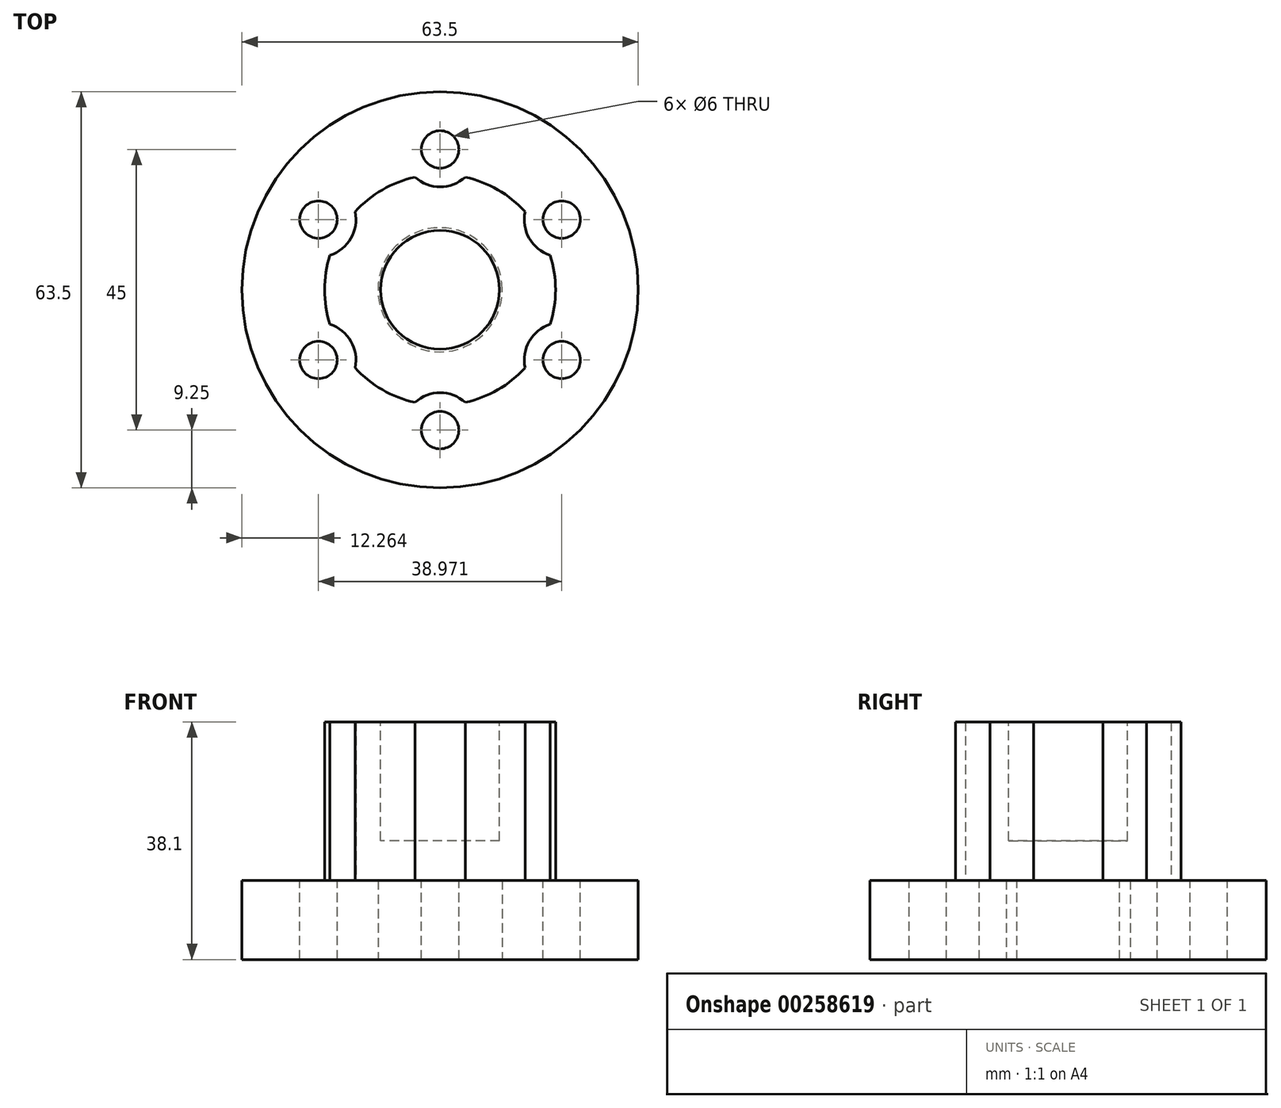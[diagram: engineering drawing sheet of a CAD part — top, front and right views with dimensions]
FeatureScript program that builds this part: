
annotation { "Feature Type Name" : "Feature", "Feature Type Description" : "" }
export const myFeature = defineFeature(function(context is Context, id is Id, definition is map)
    precondition{}
    {
        {
            var Q0;
            Q0=qCreatedBy(makeId("Top.planeOp"),FACE);
            var sketch = newSketch(context, id + "F0", { "sketchPlane" : qUnion([Q0])});
            skCircle(sketch, "E0", {"center": v(0, 0) * mm, "radius": 31.75 * mm});
            skSolve(sketch);
        }
        {
            var Q0;
            Q0=makeQuery(id+"F0.imprint","IMPRINT",FACE,{"disambiguationData":[TD([[makeQuery(id+"F0.imprint","IMPRINT",EDGE,{"derivedFrom":sQuery(id+"F0.wireOp",EDGE,"E0")}),1.0]])]});
            extrude(context, id + "F1", {"entities" : qUnion([Q0]), "depth" : 12.7 * mm});
        }
        {
            var Q0;
            Q0=makeQuery(id+"F1.opExtrude","CAP_FACE",FACE,{"disambiguationData":[OSD([sQuery(id+"F0.wireOp",EDGE,"E0")])],"isStart":false});
            var sketch = newSketch(context, id + "F2", { "sketchPlane" : qUnion([Q0])});
            skCircle(sketch, "E1", {"center": v(0, 0) * mm, "radius": 22.5 * mm, "construction": true});
            skCircle(sketch, "E2", {"center": v(0, 22.5) * mm, "radius": 3 * mm});
            skCircle(sketch, "E3.1.0", {"center": v(-19.49, 11.25) * mm, "radius": 3 * mm});
            skCircle(sketch, "E3.2.0", {"center": v(-19.49, -11.25) * mm, "radius": 3 * mm});
            skCircle(sketch, "E3.3.0", {"center": v(0, -22.5) * mm, "radius": 3 * mm});
            skCircle(sketch, "E3.4.0", {"center": v(19.49, -11.25) * mm, "radius": 3 * mm});
            skCircle(sketch, "E3.5.0", {"center": v(19.49, 11.25) * mm, "radius": 3 * mm});
            skSolve(sketch);
        }
        {
            var Q0;
            Q0 = qSketchRegion(id + "F2", true);
            extrude(context, id + "F3", {"entities" : qUnion([Q0]), "operationType" : NewBodyOperationType.REMOVE, "endBound" : BoundingType.THROUGH_ALL, "oppositeDirection" : true, "depth" : 25.4 * mm});
        }
        {
            var Q0;
            Q0=makeQuery(id+"F1.opExtrude","CAP_FACE",FACE,{"disambiguationData":[OSD([sQuery(id+"F0.wireOp",EDGE,"E0")])],"isStart":true});
            var sketch = newSketch(context, id + "F4", { "sketchPlane" : qUnion([Q0])});
            skCircle(sketch, "E4", {"center": v(0, 0) * mm, "radius": 9.95 * mm});
            skSolve(sketch);
        }
        {
            var Q0;
            Q0 = qSketchRegion(id + "F4", true);
            extrude(context, id + "F5", {"entities" : qUnion([Q0]), "operationType" : NewBodyOperationType.REMOVE, "oppositeDirection" : true, "depth" : 12.7 * mm});
        }
        {
            var Q0;
            Q0=makeQuery(id+"F1.opExtrude","CAP_FACE",FACE,{"disambiguationData":[OSD([sQuery(id+"F0.wireOp",EDGE,"E0")])],"isStart":false});
            var sketch = newSketch(context, id + "F6", { "sketchPlane" : qUnion([Q0])});
            skArc(sketch, "E5", {"start": v(4.03, -18.06) * mm, "mid": v(9.25, -16.02) * mm, "end": v(13.62, -12.52) * mm});
            skArc(sketch, "E6", {"start": v(4.03, -18.06) * mm, "mid": v(0, -16.5) * mm, "end": v(-4.03, -18.06) * mm});
            skArc(sketch, "E7.1.0", {"start": v(17.65, -5.54) * mm, "mid": v(14.29, -8.25) * mm, "end": v(13.62, -12.52) * mm});
            skArc(sketch, "E7.2.0", {"start": v(13.62, 12.52) * mm, "mid": v(14.29, 8.25) * mm, "end": v(17.65, 5.54) * mm});
            skArc(sketch, "E7.3.0", {"start": v(-4.03, 18.06) * mm, "mid": v(0, 16.5) * mm, "end": v(4.03, 18.06) * mm});
            skArc(sketch, "E7.4.0", {"start": v(-17.65, 5.54) * mm, "mid": v(-14.29, 8.25) * mm, "end": v(-13.62, 12.52) * mm});
            skArc(sketch, "E7.5.0", {"start": v(-13.62, -12.52) * mm, "mid": v(-14.29, -8.25) * mm, "end": v(-17.65, -5.54) * mm});
            skArc(sketch, "E8.trimOffspring", {"start": v(17.65, -5.54) * mm, "mid": v(18.5, 0) * mm, "end": v(17.65, 5.54) * mm});
            skArc(sketch, "E9.trimOffspring", {"start": v(13.62, 12.52) * mm, "mid": v(9.25, 16.02) * mm, "end": v(4.03, 18.06) * mm});
            skArc(sketch, "E10.trimOffspring", {"start": v(-4.03, 18.06) * mm, "mid": v(-9.25, 16.02) * mm, "end": v(-13.62, 12.52) * mm});
            skArc(sketch, "E11.trimOffspring", {"start": v(-17.65, 5.54) * mm, "mid": v(-18.5, 0) * mm, "end": v(-17.65, -5.54) * mm});
            skArc(sketch, "E12.trimOffspring", {"start": v(-13.62, -12.52) * mm, "mid": v(-9.25, -16.02) * mm, "end": v(-4.03, -18.06) * mm});
            skSolve(sketch);
        }
        {
            var Q0;
            Q0 = qSketchRegion(id + "F6", true);
            extrude(context, id + "F7", {"entities" : qUnion([Q0]), "operationType" : NewBodyOperationType.ADD, "depth" : 25.4 * mm});
        }
        {
            var Q0;
            Q0=makeQuery(id+"F7.opExtrude","CAP_FACE",FACE,{"disambiguationData":[OSD([sQuery(id+"F6.wireOp",EDGE,"E5"),sQuery(id+"F6.wireOp",EDGE,"E6"),sQuery(id+"F6.wireOp",EDGE,"E7.1.0"),sQuery(id+"F6.wireOp",EDGE,"E7.2.0"),sQuery(id+"F6.wireOp",EDGE,"E7.3.0"),sQuery(id+"F6.wireOp",EDGE,"E7.4.0"),sQuery(id+"F6.wireOp",EDGE,"E7.5.0"),sQuery(id+"F6.wireOp",EDGE,"E8.trimOffspring"),sQuery(id+"F6.wireOp",EDGE,"E9.trimOffspring"),sQuery(id+"F6.wireOp",EDGE,"E10.trimOffspring"),sQuery(id+"F6.wireOp",EDGE,"E11.trimOffspring"),sQuery(id+"F6.wireOp",EDGE,"E12.trimOffspring")])],"isStart":false});
            var sketch = newSketch(context, id + "F8", { "sketchPlane" : qUnion([Q0])});
            skCircle(sketch, "E13", {"center": v(0, 0) * mm, "radius": 9.53 * mm});
            skSolve(sketch);
        }
        {
            var Q0;
            Q0=makeQuery(id+"F8.imprint","IMPRINT",FACE,{"disambiguationData":[TD([[makeQuery(id+"F8.imprint","IMPRINT",EDGE,{"derivedFrom":sQuery(id+"F8.wireOp",EDGE,"E13")}),1.0]])]});
            extrude(context, id + "F9", {"entities" : qUnion([Q0]), "operationType" : NewBodyOperationType.REMOVE, "oppositeDirection" : true, "depth" : 19.05 * mm});
        }
    });
